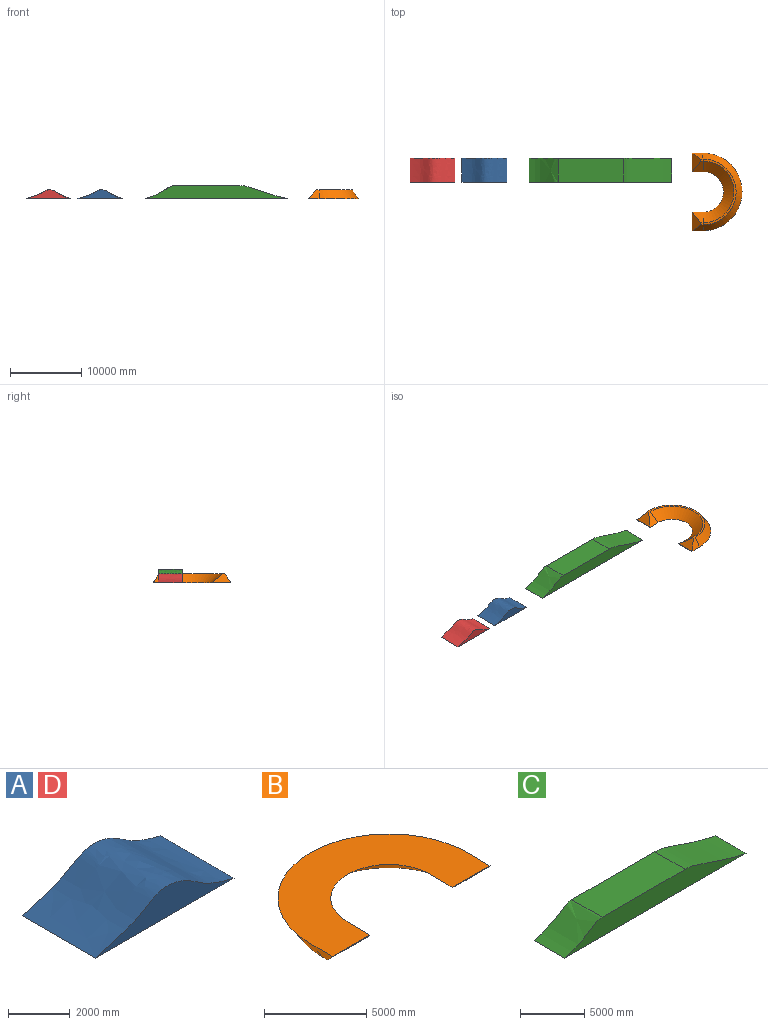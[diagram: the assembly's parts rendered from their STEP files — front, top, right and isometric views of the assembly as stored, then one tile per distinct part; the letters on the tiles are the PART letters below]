
ASSEMBLY  parts=4 mates=5
PART A: 4 faces, bbox 6323.7x3352.8x1287.4 mm
  f0: extruded ~6323.74x3352.8mm, area 22939909.1mm2, adj f1,f2,f3
  f1: plane 6323.74x3352.8mm, normal (0,0,-1), area 21202251.1mm2, adj f0,f2,f3
  f2: plane 6323.74x1287.44mm, normal (0,-1,0), area 3796995mm2, adj f0,f1
  f3: plane 6323.74x1287.44mm, normal (0,1,0), area 3796995mm2, adj f0,f1
PART B: 14 faces, bbox 10944.5x7018x1220 mm
  f0: plane 10921.14x7014.79mm, normal (0,0,1), area 41900633.8mm2, adj f1,f3,f5,f6,f7,f9,f10,f11
  f1: bspline ~8674.98x4351.29mm, area 21579644.4mm2, adj f0,f2,f6,f9
  f2: bspline ~9274.08x4649.59mm, area 4208017.5mm2, adj f1,f3,f4,f8
  f3: bspline ~10942.24x5494.17mm, area 23429444.6mm2, adj f0,f2,f5,f10
  f4: plane 333.94x302.59mm, normal (0,0,-1), area 98550.2mm2, adj f2,f5,f6,f12
  f5: plane 1534.36x1219.05mm, normal (0.83,-0.01,-0.56), area 1384073.3mm2, adj f0,f3,f4,f7,f12
  f6: plane 1524.35x1484.2mm, normal (-0.64,0.01,-0.77), area 1796498.5mm2, adj f0,f1,f4,f7,f12
  f7: plane 2594.38x32.71mm, normal (-0.01,-1,0), area 68770.7mm2, adj f0,f5,f6,f12
  f8: plane 330.08x302.62mm, normal (0,0,-1), area 98514mm2, adj f2,f9,f10,f13
  f9: plane 1523.88x1469.26mm, normal (0.64,-0.01,-0.77), area 1796326mm2, adj f0,f1,f8,f11,f13
  f10: plane 1523.88x1219.05mm, normal (-0.83,0.01,-0.56), area 1383969.6mm2, adj f0,f3,f8,f11,f13
  f11: plane 2594.58x31mm, normal (0,-1,0), area 68770.7mm2, adj f0,f9,f10,f13
  f12: plane 2541.81x1207.75mm, normal (-0.01,-0.71,-0.71), area 2397772.5mm2, adj f4,f5,f6,f7
  f13: plane 2542.01x1197.52mm, normal (0,-0.71,-0.71), area 2397722.1mm2, adj f8,f9,f10,f11
PART C: 6 faces, bbox 20015.2x3352.8x1828.8 mm
  f0: plane 9144x3352.8mm, normal (0,0,1), area 30658003.2mm2, adj f1,f3,f4,f5
  f1: extruded ~4165.6x3352.8mm, area 15389267.4mm2, adj f0,f2,f4,f5
  f2: plane 20015.2x3352.8mm, normal (0,0,-1), area 67106962.6mm2, adj f1,f3,f4,f5
  f3: extruded ~6705.6x3352.8mm, area 23369368.1mm2, adj f0,f2,f4,f5
  f4: plane 20015.2x1828.8mm, normal (0,-1,0), area 26623917.2mm2, adj f0,f1,f2,f3
  f5: plane 20015.2x1828.8mm, normal (0,1,0), area 26623917.2mm2, adj f0,f1,f2,f3
PART D: same geometry as A
PLACE A t=(-14365.6,12471.64,-5330.66)mm
PLACE B rot(axis=(-0.71,-0.71,0),180deg) t=(19504.02,3195.13,-5330.66)mm fixed
PLACE C t=(-4923.82,12471.64,-5330.66)mm
PLACE D t=(-21672.29,12471.64,-5330.66)mm
MATE planar D.f1 <-> A.f1  axis (0,0,-1) through (-18510.41,10795.24,-5330.66)mm
MATE planar A.f1 <-> C.f2  axis (0,0,-1) through (-11203.73,10795.24,-5330.66)mm
MATE planar C.f5 <-> A.f3  axis (0,1,0) through (-758.22,12471.64,-3501.86)mm
MATE planar C.f2 <-> B.f0  axis (0,0,-1) through (15091.38,10795.24,-5330.66)mm
MATE planar D.f3 <-> A.f3  axis (0,1,0) through (-18436.29,12471.64,-4893.09)mm
